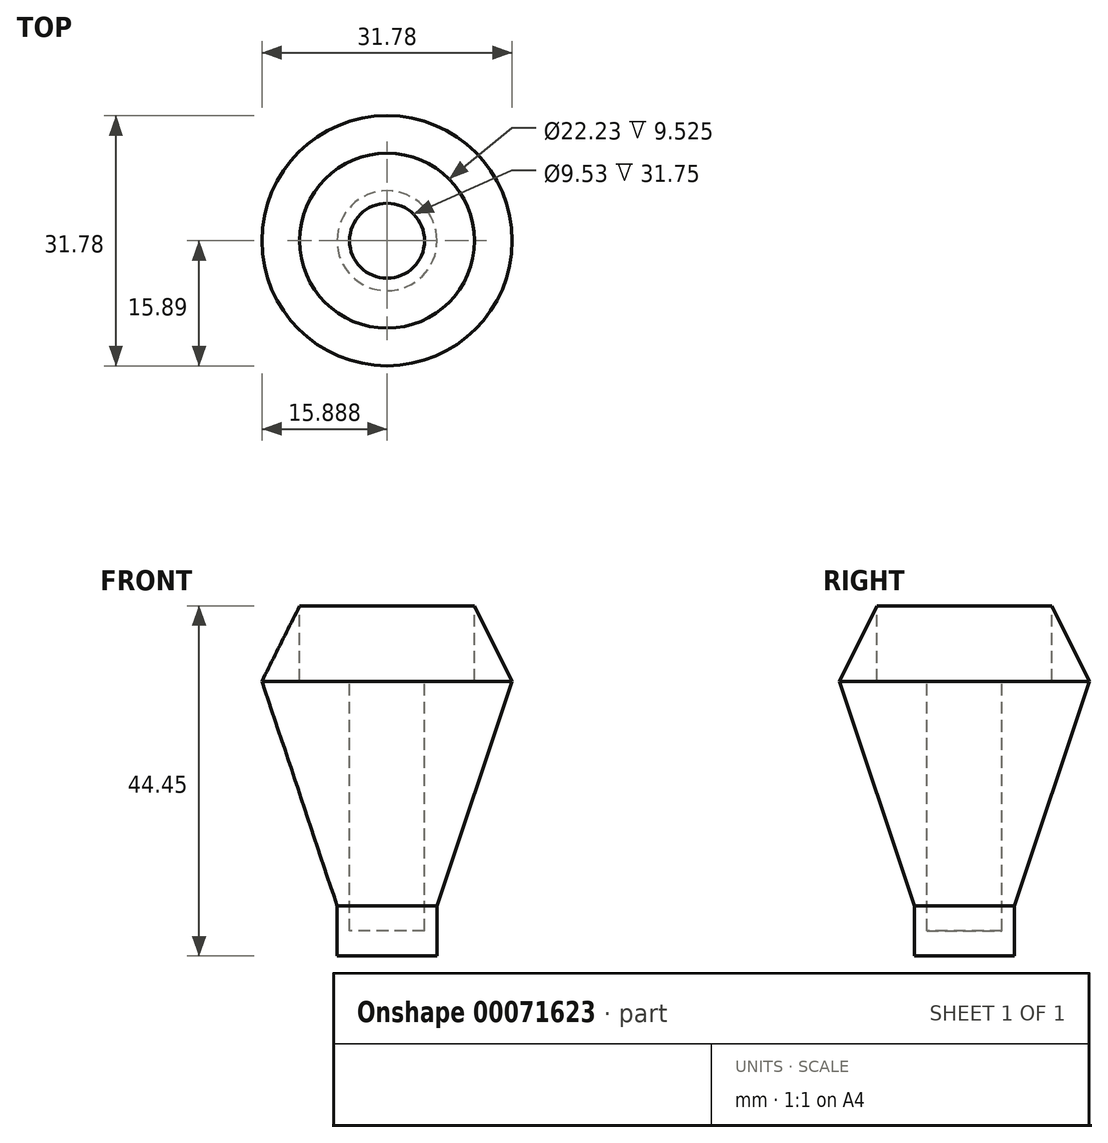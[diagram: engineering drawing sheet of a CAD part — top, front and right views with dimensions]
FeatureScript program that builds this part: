
annotation { "Feature Type Name" : "Feature", "Feature Type Description" : "" }
export const myFeature = defineFeature(function(context is Context, id is Id, definition is map)
    precondition{}
    {
        {
            var Q0;
            Q0=qCreatedBy(makeId("Top.planeOp"),FACE);
            var sketch = newSketch(context, id + "F0", { "sketchPlane" : qUnion([Q0])});
            skCircle(sketch, "E0", {"center": v(-69.47, -28.08) * mm, "radius": 6.35 * mm});
            skSolve(sketch);
        }
        {
            var Q0;
            Q0 = qSketchRegion(id + "F0", true);
            extrude(context, id + "F1", {"entities" : qUnion([Q0]), "depth" : 6.35 * mm});
        }
        {
            var Q0;
            Q0=makeQuery(id+"F1.opExtrude","CAP_FACE",FACE,{"disambiguationData":[OSD([sQuery(id+"F0.wireOp",EDGE,"E0")])],"isStart":false});
            var sketch = newSketch(context, id + "F2", { "sketchPlane" : qUnion([Q0])});
            skCircle(sketch, "E1", {"center": v(-69.47, -28.08) * mm, "radius": 15.88 * mm});
            skSolve(sketch);
        }
        {
            var Q0;
            Q0 = qSketchRegion(id + "F2", true);
            extrude(context, id + "F3", {"entities" : qUnion([Q0]), "operationType" : NewBodyOperationType.ADD, "depth" : 44.45 * mm});
        }
        {
            var Q0;
            Q0=makeQuery(id+"F3.opExtrude","SWEPT_FACE",FACE,{"disambiguationData":[OSD([sQuery(id+"F2.wireOp",EDGE,"E1")])]});
            chamfer(context, id + "F4", {"entities" : qUnion([Q0]), "width" : 5.08 * mm, "tangentPropagation" : true});
        }
        {
            var Q0;
            Q0=makeQuery(id+"F3.opExtrude","SWEPT_FACE",FACE,{"disambiguationData":[OSD([sQuery(id+"F2.wireOp",EDGE,"E1")])]});
            chamfer(context, id + "F5", {"entities" : qUnion([Q0]), "width" : 5.08 * mm, "tangentPropagation" : true});
        }
        {
            var Q0;
            Q0=makeQuery(id+"F3.opExtrude","CAP_FACE",FACE,{"disambiguationData":[OSD([sQuery(id+"F2.wireOp",EDGE,"E1")])],"isStart":false});
            var sketch = newSketch(context, id + "F6", { "sketchPlane" : qUnion([Q0])});
            skCircle(sketch, "E2", {"center": v(-69.47, -28.08) * mm, "radius": 10.63 * mm});
            skSolve(sketch);
        }
        {
            var Q0;
            Q0 = qSketchRegion(id + "F6", true);
            extrude(context, id + "F7", {"entities" : qUnion([Q0]), "operationType" : NewBodyOperationType.REMOVE, "oppositeDirection" : true, "depth" : 6.35 * mm});
        }
        {
            var Q0;
            Q0=makeQuery(id+"F7.boolean.opBoolean","COPY",FACE,{"derivedFrom":makeQuery(id+"F7.opExtrude","CAP_FACE",FACE,{"disambiguationData":[OSD([sQuery(id+"F6.wireOp",EDGE,"E2")])],"isStart":false})});
            var sketch = newSketch(context, id + "F8", { "sketchPlane" : qUnion([Q0])});
            skCircle(sketch, "E3", {"center": v(-69.47, -28.08) * mm, "radius": 4.76 * mm});
            skSolve(sketch);
        }
        {
            var Q0;
            Q0 = qSketchRegion(id + "F8", true);
            extrude(context, id + "F9", {"entities" : qUnion([Q0]), "operationType" : NewBodyOperationType.REMOVE, "oppositeDirection" : true, "depth" : 31.75 * mm});
        }
        {
            var Q0;
            Q0=makeQuery(id+"F1.opExtrude","SWEPT_BODY",BODY,{"disambiguationData":[OSD([sQuery(id+"F0.wireOp",EDGE,"E0")])]});
            deleteBodies(context, id + "F10", {"entities" : qUnion([Q0])});
        }
        {
            var Q0;
            Q0=qCreatedBy(makeId("Top.planeOp"),FACE);
            var sketch = newSketch(context, id + "F11", { "sketchPlane" : qUnion([Q0])});
            skCircle(sketch, "E4", {"center": v(-63.75, -45.28) * mm, "radius": 6.35 * mm});
            skSolve(sketch);
        }
        {
            var Q0;
            Q0 = qSketchRegion(id + "F11", true);
            extrude(context, id + "F12", {"entities" : qUnion([Q0]), "depth" : 6.35 * mm});
        }
        {
            var Q0;
            Q0=makeQuery(id+"F12.opExtrude","CAP_FACE",FACE,{"disambiguationData":[OSD([sQuery(id+"F11.wireOp",EDGE,"E4")])],"isStart":false});
            var sketch = newSketch(context, id + "F13", { "sketchPlane" : qUnion([Q0])});
            skCircle(sketch, "E5", {"center": v(-63.75, -45.28) * mm, "radius": 6.35 * mm});
            skSolve(sketch);
        }
        {
            var Q0;
            Q0 = qSketchRegion(id + "F13", true);
            extrude(context, id + "F14", {"entities" : qUnion([Q0]), "operationType" : NewBodyOperationType.ADD, "depth" : 31.75 * mm});
        }
        {
            var Q0;
            Q0=makeQuery(id+"F14.opExtrude","CAP_FACE",FACE,{"disambiguationData":[OSD([sQuery(id+"F13.wireOp",EDGE,"E5")])],"isStart":false});
            var sketch = newSketch(context, id + "F15", { "sketchPlane" : qUnion([Q0])});
            skCircle(sketch, "E6", {"center": v(-63.75, -45.28) * mm, "radius": 15.88 * mm});
            skSolve(sketch);
        }
        {
            var Q0;
            Q0 = qSketchRegion(id + "F15", true);
            extrude(context, id + "F16", {"entities" : qUnion([Q0]), "operationType" : NewBodyOperationType.ADD, "depth" : 6.35 * mm});
        }
        {
            var Q0;
            Q0=qCreatedBy(makeId("Front.planeOp"),FACE);
            var sketch = newSketch(context, id + "F17", { "sketchPlane" : qUnion([Q0])});
            skLineSegment(sketch, "E7", {"start": v(23.36, 39.54) * mm, "end": v(32.9, 11) * mm});
            skLineSegment(sketch, "E8", {"start": v(32.9, 11) * mm, "end": v(32.9, 4.65) * mm});
            skLineSegment(sketch, "E9", {"start": v(32.9, 4.65) * mm, "end": v(39.25, 4.65) * mm});
            skLineSegment(sketch, "E10", {"start": v(39.25, 4.65) * mm, "end": v(39.25, 49.1) * mm});
            skLineSegment(sketch, "E11", {"start": v(39.25, 49.1) * mm, "end": v(28.14, 49.1) * mm});
            skLineSegment(sketch, "E12", {"start": v(28.14, 49.1) * mm, "end": v(23.36, 39.54) * mm});
            skSolve(sketch);
        }
        {
            var Q0;
            Q0 = qSketchRegion(id + "F17", true);
            var Q1;
            Q1=sQuery(id+"F17.wireOp",EDGE,"E10");
            revolve(context, id + "F18", {"entities" : qUnion([Q0]), "axis" : qUnion([Q1]), "revolveType" : RevolveType.FULL});
        }
        {
            var Q0;
            Q0=makeQuery(id+"F12.opExtrude","SWEPT_BODY",BODY,{"disambiguationData":[OSD([sQuery(id+"F11.wireOp",EDGE,"E4")])]});
            deleteBodies(context, id + "F19", {"entities" : qUnion([Q0])});
        }
        {
            var Q0;
            Q0=makeQuery(id+"F18.opRevolve","SWEPT_FACE",FACE,{"disambiguationData":[OSD([sQuery(id+"F17.wireOp",EDGE,"E11")])]});
            var sketch = newSketch(context, id + "F20", { "sketchPlane" : qUnion([Q0])});
            skCircle(sketch, "E13", {"center": v(39.25, 0) * mm, "radius": 11.11 * mm});
            skSolve(sketch);
        }
        {
            var Q0;
            Q0 = qSketchRegion(id + "F20", true);
            extrude(context, id + "F21", {"entities" : qUnion([Q0]), "operationType" : NewBodyOperationType.REMOVE, "oppositeDirection" : true, "depth" : 9.52 * mm});
        }
        {
            var Q0;
            Q0=makeQuery(id+"F21.boolean.opBoolean","COPY",FACE,{"derivedFrom":makeQuery(id+"F21.opExtrude","CAP_FACE",FACE,{"disambiguationData":[OSD([sQuery(id+"F20.wireOp",EDGE,"E13")])],"isStart":false})});
            var sketch = newSketch(context, id + "F22", { "sketchPlane" : qUnion([Q0])});
            skCircle(sketch, "E14", {"center": v(39.25, 0) * mm, "radius": 4.76 * mm});
            skSolve(sketch);
        }
        {
            var Q0;
            Q0 = qSketchRegion(id + "F22", true);
            extrude(context, id + "F23", {"entities" : qUnion([Q0]), "operationType" : NewBodyOperationType.REMOVE, "oppositeDirection" : true, "depth" : 31.75 * mm});
        }
    });
